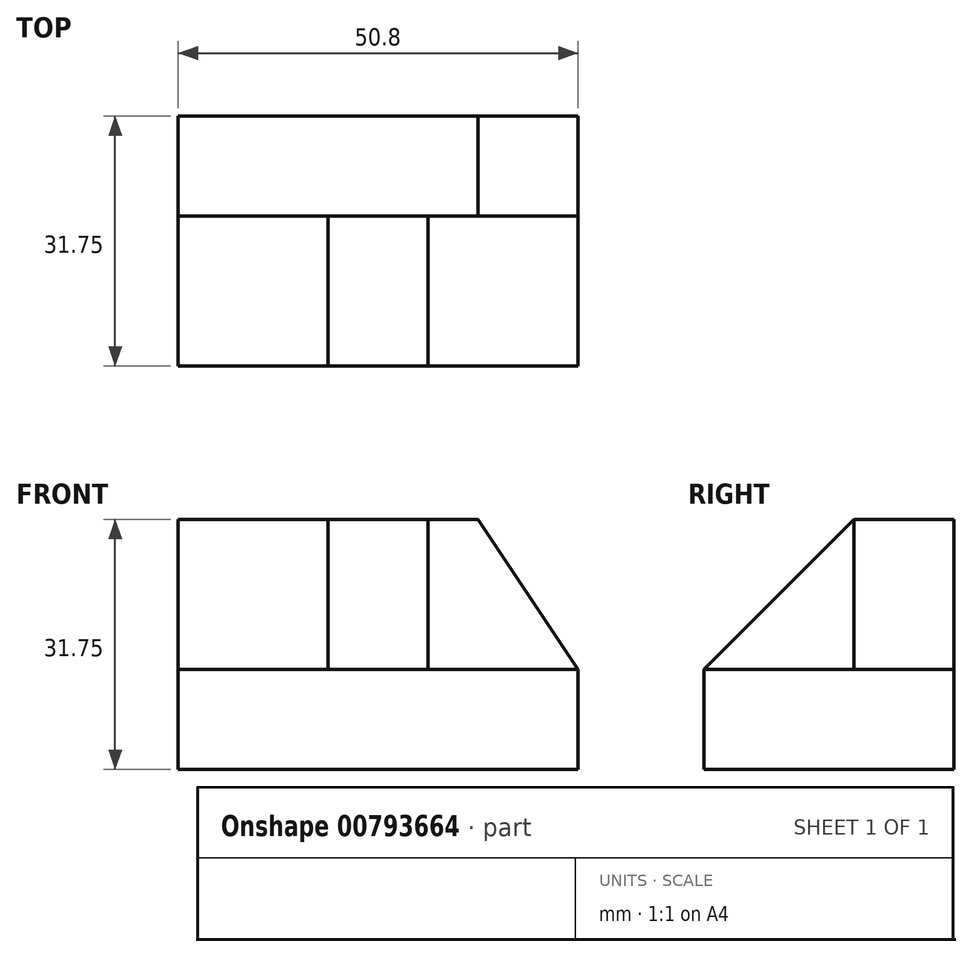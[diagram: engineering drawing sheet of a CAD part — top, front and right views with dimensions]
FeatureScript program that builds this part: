
annotation { "Feature Type Name" : "Feature", "Feature Type Description" : "" }
export const myFeature = defineFeature(function(context is Context, id is Id, definition is map)
    precondition{}
    {
        {
            var Q0;
            Q0=qCreatedBy(makeId("Right.planeOp"),FACE);
            var sketch = newSketch(context, id + "F0", { "sketchPlane" : qUnion([Q0])});
            skLineSegment(sketch, "E0", {"start": v(0, 0) * mm, "end": v(0, 31.75) * mm});
            skLineSegment(sketch, "E1", {"start": v(0, 31.75) * mm, "end": v(-31.75, 31.75) * mm});
            skLineSegment(sketch, "E2", {"start": v(-31.75, 31.75) * mm, "end": v(-31.75, 0) * mm});
            skLineSegment(sketch, "E3", {"start": v(-31.75, 0) * mm, "end": v(0, 0) * mm});
            skSolve(sketch);
        }
        {
            var Q0;
            Q0=makeQuery(id+"F0.imprint","IMPRINT",FACE,{"disambiguationData":[TD([[makeQuery(id+"F0.imprint","IMPRINT",EDGE,{"derivedFrom":sQuery(id+"F0.wireOp",EDGE,"E0")}),1.0]])]});
            extrude(context, id + "F1", {"entities" : qUnion([Q0]), "depth" : 50.8 * mm, "offsetDistance" : 25.4 * mm});
        }
        {
            var Q0;
            Q0=makeQuery(id+"F1.opExtrude","CAP_FACE",FACE,{"disambiguationData":[OSD([sQuery(id+"F0.wireOp",EDGE,"E0"),sQuery(id+"F0.wireOp",EDGE,"E1"),sQuery(id+"F0.wireOp",EDGE,"E2"),sQuery(id+"F0.wireOp",EDGE,"E3")])],"isStart":false});
            var sketch = newSketch(context, id + "F2", { "sketchPlane" : qUnion([Q0])});
            skLineSegment(sketch, "E4", {"start": v(-31.75, 12.7) * mm, "end": v(-12.7, 12.7) * mm});
            skLineSegment(sketch, "E5", {"start": v(-12.7, 12.7) * mm, "end": v(-12.7, 31.75) * mm});
            skLineSegment(sketch, "E6", {"start": v(-12.7, 31.75) * mm, "end": v(-31.75, 31.75) * mm});
            skLineSegment(sketch, "E7", {"start": v(-31.75, 31.75) * mm, "end": v(-31.75, 12.7) * mm});
            skSolve(sketch);
        }
        {
            var Q0;
            Q0=qSketchRegion(id+"F2",true);
            extrude(context, id + "F3", {"entities" : qUnion([Q0]), "operationType" : NewBodyOperationType.REMOVE, "oppositeDirection" : true, "depth" : 19.05 * mm, "offsetDistance" : 25.4 * mm});
        }
        {
            var Q0;
            Q0=makeQuery(id+"F3.boolean.opBoolean","COPY",FACE,{"derivedFrom":makeQuery(id+"F3.opExtrude","CAP_FACE",FACE,{"disambiguationData":[OSD([sQuery(id+"F2.wireOp",EDGE,"E4"),sQuery(id+"F2.wireOp",EDGE,"E5"),sQuery(id+"F2.wireOp",EDGE,"E6"),sQuery(id+"F2.wireOp",EDGE,"E7")])],"isStart":false})});
            var sketch = newSketch(context, id + "F4", { "sketchPlane" : qUnion([Q0])});
            skLineSegment(sketch, "E8", {"start": v(-12.7, 31.75) * mm, "end": v(-31.75, 12.7) * mm});
            skLineSegment(sketch, "E9", {"start": v(-31.75, 12.7) * mm, "end": v(-31.75, 31.75) * mm});
            skLineSegment(sketch, "E10", {"start": v(-31.75, 31.75) * mm, "end": v(-12.7, 31.75) * mm});
            skSolve(sketch);
        }
        {
            var Q0;
            Q0=makeQuery(id+"F4.imprint","IMPRINT",FACE,{"disambiguationData":[TD([[makeQuery(id+"F4.imprint","IMPRINT",EDGE,{"derivedFrom":sQuery(id+"F4.wireOp",EDGE,"E8")}),-1.0]])]});
            extrude(context, id + "F5", {"entities" : qUnion([Q0]), "operationType" : NewBodyOperationType.REMOVE, "oppositeDirection" : true, "depth" : 12.7 * mm, "offsetDistance" : 25.4 * mm});
        }
        {
            var Q0;
            Q0=makeQuery(id+"F1.opExtrude","CAP_FACE",FACE,{"disambiguationData":[OSD([sQuery(id+"F0.wireOp",EDGE,"E0"),sQuery(id+"F0.wireOp",EDGE,"E1"),sQuery(id+"F0.wireOp",EDGE,"E2"),sQuery(id+"F0.wireOp",EDGE,"E3")])],"isStart":true});
            var sketch = newSketch(context, id + "F6", { "sketchPlane" : qUnion([Q0])});
            skLineSegment(sketch, "E11", {"start": v(31.75, 31.75) * mm, "end": v(12.7, 31.75) * mm});
            skLineSegment(sketch, "E12", {"start": v(12.7, 31.75) * mm, "end": v(12.7, 12.7) * mm});
            skLineSegment(sketch, "E13", {"start": v(12.7, 12.7) * mm, "end": v(31.75, 12.7) * mm});
            skLineSegment(sketch, "E14", {"start": v(31.75, 12.7) * mm, "end": v(31.75, 31.75) * mm});
            skSolve(sketch);
        }
        {
            var Q0;
            Q0=makeQuery(id+"F6.imprint","IMPRINT",FACE,{"disambiguationData":[TD([[makeQuery(id+"F6.imprint","IMPRINT",EDGE,{"derivedFrom":sQuery(id+"F6.wireOp",EDGE,"E11")}),-1.0]])]});
            extrude(context, id + "F7", {"entities" : qUnion([Q0]), "operationType" : NewBodyOperationType.REMOVE, "oppositeDirection" : true, "depth" : 19.05 * mm, "offsetDistance" : 25.4 * mm});
        }
        {
            var Q0;
            Q0=makeQuery(id+"F3.boolean.opBoolean","COPY",FACE,{"derivedFrom":makeQuery(id+"F3.opExtrude","SWEPT_FACE",FACE,{"disambiguationData":[OSD([sQuery(id+"F2.wireOp",EDGE,"E5")])]})});
            var sketch = newSketch(context, id + "F8", { "sketchPlane" : qUnion([Q0])});
            skLineSegment(sketch, "E15", {"start": v(50.8, 12.7) * mm, "end": v(38.1, 31.75) * mm});
            skSolve(sketch);
        }
        {
            var Q0;
            {var subQ0=sQuery(id+"F8.wireOp",EDGE,"E15");Q0=makeQuery(id+"F8.imprint","IMPRINT",FACE,{"disambiguationData":[TD([[makeQuery(id+"F8.imprint","IMPRINT",EDGE,{"derivedFrom":subQ0}),-1.0]])]});}
            extrude(context, id + "F9", {"entities" : qUnion([Q0]), "operationType" : NewBodyOperationType.REMOVE, "oppositeDirection" : true, "depth" : 12.7 * mm, "offsetDistance" : 25.4 * mm});
        }
    });
